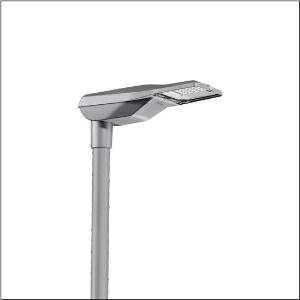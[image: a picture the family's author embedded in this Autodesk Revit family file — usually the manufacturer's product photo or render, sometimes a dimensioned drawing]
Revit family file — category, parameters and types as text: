
# Revit family: streetlight_sl_21_iq_micro___st1_5a_5xe1p41g08cb_60b9
name_source: partatom
category: Lighting Fixtures
units: mm (PartAtom-declared; Revit-internal decimal feet)

## family parameters
Cut with Voids When Loaded = No
Host = Face
Light Source = No
Part Type = Normal
Room Calculation Point = No
Round Connector Dimension = Use Diameter
Shared = No

## types (1)
- --- (1 x LED, 2930 lm, 19.4 W, 4000K)
    Apparent Load = 19 VA
    CIE Flux Codes = 22 53 95 100 100
    Color Rendering = 70
    Color Temperature = 4000K
    Default Elevation = 1800 mm
    Description = Streetlight SL 21 iQ micro, mast luminaire, primary light control with lens, of PMMA, primary optical cover: cover, of toughened safety glass, transparent, light distribution: ST1.5a, light emission: direct distribution, primary light characteristic: asymmetric, installation type: post-top, side-entry, LED, High Power LED, rated luminous flux: 2.930lm, luminous efficacy: 151lm/W, light colour: 740, colour temperature: 4000K, control: Street-Remote, Auto-Match, Temp-Guard, Lumen-Switch, Night-Set, Smart-Wire, Light-Fading, Desk-Remote (wireless, voltage-free reading and setting of iQ features in the workshop via application-optimized NFC function/RFID function), optimised constant luminous flux control (CLO 2.0), presetting dimming linear, mains connection: 220..240V, AC, 50/60Hz, start of lifetime: 19W, end of service life: 20W, reduction: 10W, luminaire housing, of diecast aluminium, powder-coated, Siteco® metallic grey (DB 702S), corrosivity category C5 mid according to DIN EN ISO 12944, please order mast flange separately, inclination adjustable: 0°, 5°, 10°, 15°, sealing non-destructively replaceable, multi-level sealing system, length: 528mm, width: 235mm, height: 110mm, mast flange for spigot size: 42mm (side-entry): 5XC10008XM4, 60/48mm (side-entry/post-top): 5XC10108XM2, 76/60mm (side-entry/post-top): 5XC10108XM1, protection rating (complete): IP66, insulation class (complete): insulation class II (safety insulation), certification: CE, ENEC, ENEC+, VDE, impact resistance: IK09, permissible operating ambient temperature for outdoor applications: -40..+50°C, standard-compliant lighting for roads and squares, packaging unit: 1 piece

Light Distribution: ST1.5a
    Height = 110 mm
    Lamp = 1 x LED
    Lamp Light Flux = 2930 lm
    Lamp Power = 19.4 W
    Lamp count = 1
    Length = 528 mm
    Luminous efficacy = 151 lm/W
    Manufacturer = Siteco
    ModVariant = No
    Model = 5XE1P41G08CB
    Number of Poles = 1
    OnlyDefault = Yes
    Power Factor = 1
    Product Name = Streetlight SL 21 iQ micro | ST1.5a
    Product group = mast luminaire | pylon top
    ProductGroupID = 6100
    Protection Class = Protection class II
    Protection Degree = IP 66
    RLX_Detail_Level = 1
    RLX_Emergency_Light_Flux = 0 lm
    RLX_Emergency_Type = 0
    RLX_Emergency_Type_DB = No
    RlxData = <blob elided: 102733 chars, md5=2cf2b3b4>
    Socket = socket
    Standby Power = 0 W
    System Light Flux = 2930 lm
    System Power = 19 W
    Type Comments = factory setting: luminous flux: 100 % | dim-lin: 254 | 387 mA
    Type Image = l_1006881.jpg
    URL = http://relux.com
    VarID = @adj_069325
    Voltage = 0 V
    Weight = 0.00 kg
    Width = 235 mm

## geometry (parser evidence)
native form markers: Blend x4, Sweep x9
no freeform markers — native parametric forms only
